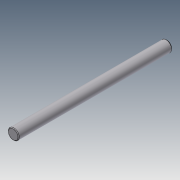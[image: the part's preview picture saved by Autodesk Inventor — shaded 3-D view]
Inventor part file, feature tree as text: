
AUTODESK INVENTOR PART (.ipt)
format: ipt  version: 2018.3 (Build 223284000, 284)  size: 108,032 bytes
history: native  units: in
note: dims shown in document units (in); Inventor stores cm internally (conversion verified against a paired STEP export)
features: hole x2, sketch x2, extrude x1, chamfer x1
ambient origin geometry x8: Origin, YZ Plane, XZ Plane, XY Plane, X Axis, Y Axis, Z Axis, Center Point
bodies: Solid1 (feature_tree)
feature tree (6):
  extrude  "Extrusion1"  Depth=3.52in TaperAngle=0.0deg
  hole  "Hole2"  [1 undecoded]
  chamfer  "Chamfer3"  [1 undecoded]
  hole  "Hole3"  [1 undecoded]
  sketch  "Sketch1"  dims[d0=0.25in d1=3.52in d2=0.0in]
  sketch  "Sketch11"  dims[d32=0.015in d33=0.015in d34=45.0deg d63=1.0in d64=1.0in d56=0.158in d57=0.75in d58=0.178in d59=0.25in d60=90.0deg d61=1.15in d62=0.8108in d65=0.06in d66=0.06in d67=0.75in d68=0.375in d69=0.25in d70=0.5635in d71=0.15in d72=0.8108in]
note: 3 required parameter values undecoded (feature->parameter linkage not recoverable at this tier; creation-order binding heuristic only, values carry confidence <= 0.55)
